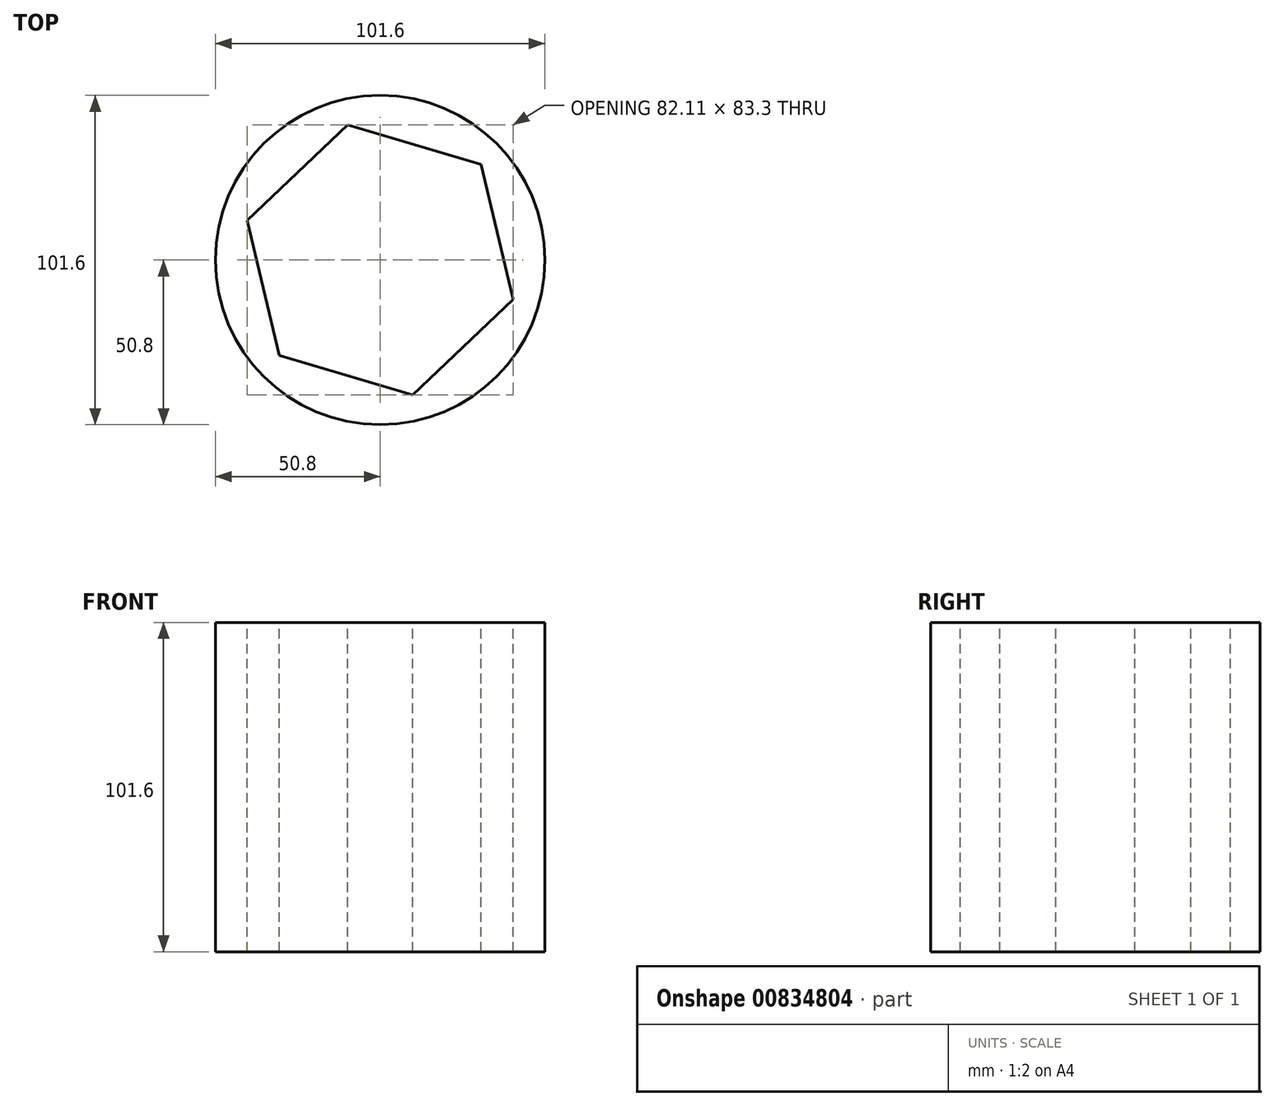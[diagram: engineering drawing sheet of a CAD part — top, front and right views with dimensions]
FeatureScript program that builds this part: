
annotation { "Feature Type Name" : "Feature", "Feature Type Description" : "" }
export const myFeature = defineFeature(function(context is Context, id is Id, definition is map)
    precondition{}
    {
        {
            var Q0;
            Q0=qCreatedBy(makeId("Top.planeOp"),FACE);
            var sketch = newSketch(context, id + "F0", { "sketchPlane" : qUnion([Q0])});
            skCircle(sketch, "E0", {"center": v(0, 0) * mm, "radius": 50.8 * mm});
            skSolve(sketch);
        }
        {
            var Q0;
            Q0=makeQuery(id+"F0.imprint","IMPRINT",FACE,{"disambiguationData":[TD([[makeQuery(id+"F0.imprint","IMPRINT",EDGE,{"derivedFrom":sQuery(id+"F0.wireOp",EDGE,"E0")}),1.0]])]});
            extrude(context, id + "F1", {"entities" : qUnion([Q0]), "depth" : 101.6 * mm, "offsetDistance" : 25.4 * mm});
        }
        {
            var Q0;
            Q0=makeQuery(id+"F1.opExtrude","CAP_FACE",FACE,{"disambiguationData":[OSD([sQuery(id+"F0.wireOp",EDGE,"E0")])],"isStart":false});
            var sketch = newSketch(context, id + "F2", { "sketchPlane" : qUnion([Q0])});
            skCircle(sketch, "E1.cCircle", {"center": v(0, 0) * mm, "radius": 42.83 * mm, "construction": true});
            skLineSegment(sketch, "E1.0", {"start": v(41.06, -12.19) * mm, "end": v(9.97, -41.65) * mm});
            skLineSegment(sketch, "E1.1", {"start": v(9.97, -41.65) * mm, "end": v(-31.08, -29.46) * mm});
            skLineSegment(sketch, "E1.2", {"start": v(-31.08, -29.46) * mm, "end": v(-41.06, 12.19) * mm});
            skLineSegment(sketch, "E1.3", {"start": v(-41.06, 12.19) * mm, "end": v(-9.97, 41.65) * mm});
            skLineSegment(sketch, "E1.4", {"start": v(-9.97, 41.65) * mm, "end": v(31.08, 29.46) * mm});
            skLineSegment(sketch, "E1.5", {"start": v(31.08, 29.46) * mm, "end": v(41.06, -12.19) * mm});
            skSolve(sketch);
        }
        {
            var Q0;
            Q0=makeQuery(id+"F2.imprint","IMPRINT",FACE,{"disambiguationData":[TD([[makeQuery(id+"F2.imprint","IMPRINT",EDGE,{"derivedFrom":sQuery(id+"F2.wireOp",EDGE,"E1.0")}),-1.0]])]});
            extrude(context, id + "F3", {"entities" : qUnion([Q0]), "operationType" : NewBodyOperationType.REMOVE, "oppositeDirection" : true, "depth" : 135.13 * mm, "offsetDistance" : 25.4 * mm});
        }
    });
